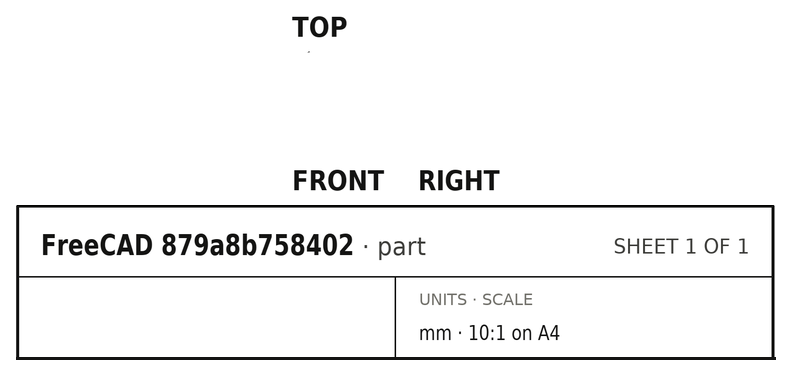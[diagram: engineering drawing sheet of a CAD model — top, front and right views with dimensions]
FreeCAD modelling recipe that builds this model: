
FCSTD DOCUMENT  (FreeCAD 0.21R33694 (Git))
Label: coax
License: All rights reserved
LicenseURL: http://en.wikipedia.org/wiki/All_rights_reserved
objects: Part::Part2DObjectPython×5, App::FeaturePython×3, Part::Cut×1, Part::MultiCommon×1
note: 7 computed .brp shape members not serialized (recipe doc carries the construction recipe); baked Part::Feature solids carry a one-line shape summary decoded from their .brp

FEATURE [Part::Part2DObjectPython] Circle  # Draft 2D object (typed FeaturePython)
  Area = 6.88134e-06
  FirstAngle = 0
  LastAngle = 0
  MakeFace = true
  Radius = 0.00148
FEATURE [Part::Part2DObjectPython] Circle001  # Draft 2D object (typed FeaturePython)
  Area = 5.17848e-07
  FirstAngle = 0
  LastAngle = 0
  MakeFace = true
  Radius = 0.000406
FEATURE [Part::Cut] Cut
  Base = -> Circle
  Tool = -> Circle001
FEATURE [Part::Part2DObjectPython] Line  label="_P1"  # Draft 2D object (typed FeaturePython)
  Area = 0
  ChamferSize = 0
  Closed = false
  End = (0.00148,0,0)
  FilletRadius = 0
  Length = 0.001074
  MakeFace = true
  Placement = pos=(0.000406,0,0) rot=(0,0,1;0rad)
  Points = (2) [(0,0,0),(0.001074,0,0)]
  Start = (0.000406,0,0)
  Subdivisions = 0
FEATURE [App::FeaturePython] Text  label="_M1(voltage){1}"  # WARN: FeaturePython — macro-defined, semantics opaque (R4)
  Placement = pos=(0.000624029,-0.00216561,0) rot=(0,0,1;0rad)
  Text = .
FEATURE [Part::Part2DObjectPython] Wire  # Draft 2D object (typed FeaturePython)
  Area = 5e-05
  ChamferSize = 0
  Closed = true
  End = (0,0,0)
  FilletRadius = 0
  Length = 0.0341421
  MakeFace = true
  Points = (4) [(0,0,0),(0.01,3.06162e-19,0),(0.01,0.01,0),(0,0,0)]
  Start = (0,0,0)
  Subdivisions = 0
FEATURE [Part::MultiCommon] Common  label="slice"
  Shapes = -> [Cut,Wire]
FEATURE [Part::Part2DObjectPython] Line001  label="_P2"  # Draft 2D object (typed FeaturePython)
  Area = 0
  ChamferSize = 0
  Closed = false
  End = (0.00104652,0.00104652,0)
  FilletRadius = 0
  Length = 0.001074
  MakeFace = true
  Placement = pos=(0.000287085,0.000287085,0) rot=(0,0,1;0rad)
  Points = (2) [(0,0,0),(0.000759433,0.000759433,0)]
  Start = (0.000287085,0.000287085,0)
  Subdivisions = 0
FEATURE [App::FeaturePython] Text001  label="_B1(PMC){1}"  # WARN: FeaturePython — macro-defined, semantics opaque (R4)
  Placement = pos=(0.00119715,-0.000671772,0) rot=(0,0,1;0rad)
  Text = .
FEATURE [App::FeaturePython] Text002  label="_B2(PMC){2}"  # WARN: FeaturePython — macro-defined, semantics opaque (R4)
  Placement = pos=(0.00124922,-0.000408862,0) rot=(0,0,1;0rad)
  Text = .
